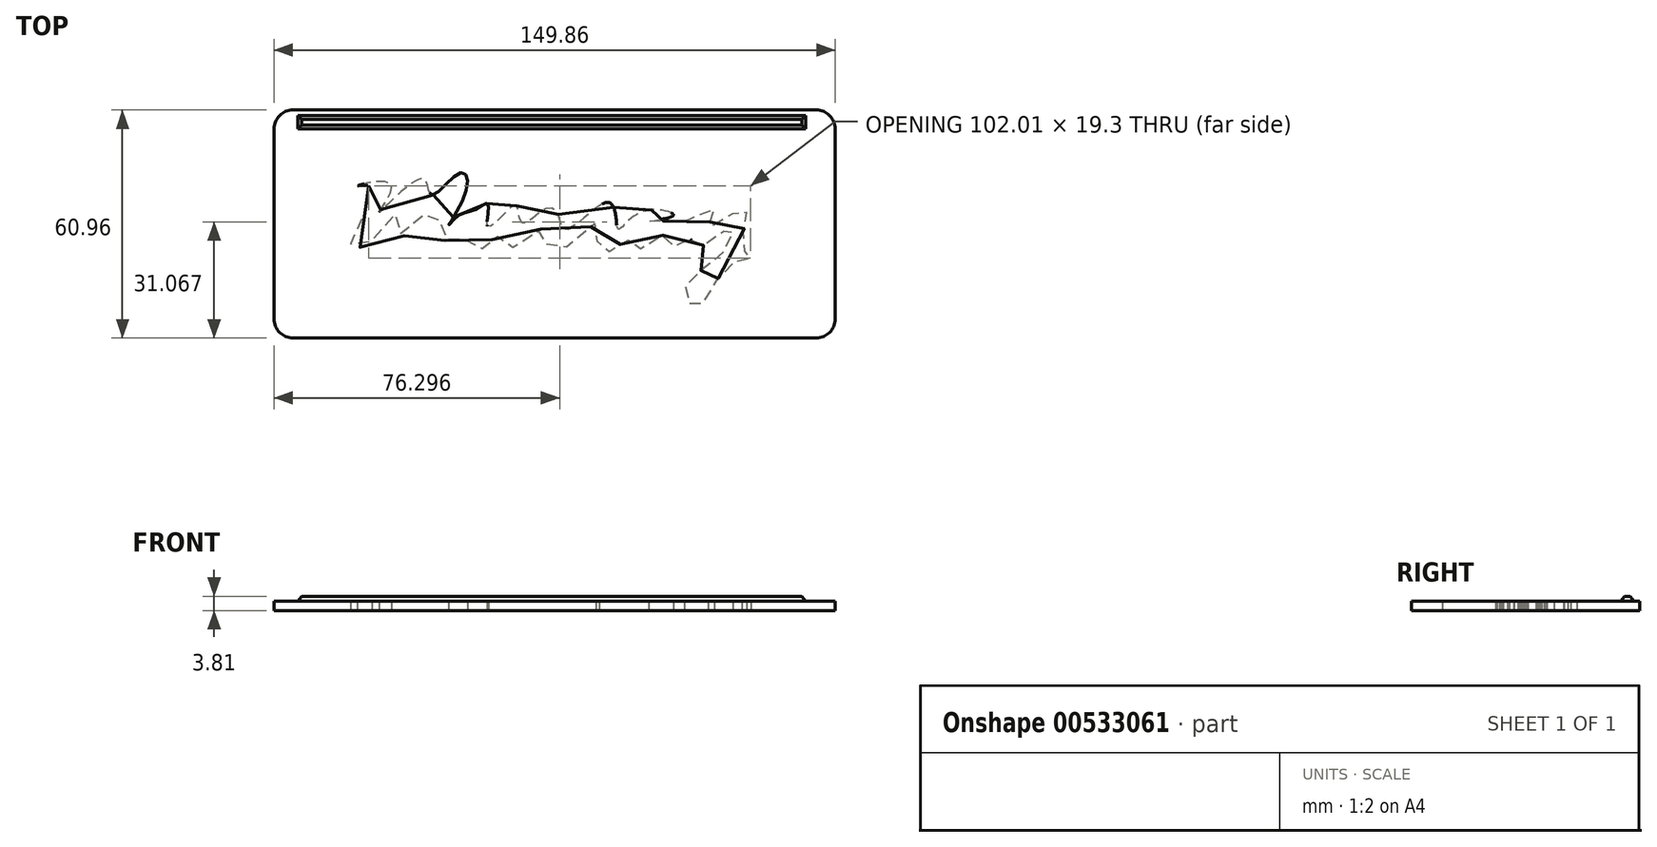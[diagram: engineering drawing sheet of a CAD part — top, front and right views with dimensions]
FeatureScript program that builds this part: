
annotation { "Feature Type Name" : "Feature", "Feature Type Description" : "" }
export const myFeature = defineFeature(function(context is Context, id is Id, definition is map)
    precondition{}
    {
        {
            var Q0;
            Q0=qCreatedBy(makeId("Top.planeOp"),FACE);
            var sketch = newSketch(context, id + "F0", { "sketchPlane" : qUnion([Q0])});
            skLineSegment(sketch, "E0.bottom", {"start": v(69.85, -25.4) * mm, "end": v(-69.85, -25.4) * mm, "construction": true});
            skLineSegment(sketch, "E0.top", {"start": v(69.85, 25.4) * mm, "end": v(-69.85, 25.4) * mm, "construction": true});
            skLineSegment(sketch, "E0.left", {"start": v(69.85, -25.4) * mm, "end": v(69.85, 25.4) * mm, "construction": true});
            skLineSegment(sketch, "E0.right", {"start": v(-69.85, -25.4) * mm, "end": v(-69.85, 25.4) * mm, "construction": true});
            skPoint(sketch, "E0.middle", {"position": v(0, 0) * mm});
            skArc(sketch, "E1", {"start": v(-64.77, 25.4) * mm, "mid": v(-73.44, 29) * mm, "end": v(-69.85, 20.32) * mm});
            skArc(sketch, "E2", {"start": v(69.85, 20.32) * mm, "mid": v(73.44, 29) * mm, "end": v(64.77, 25.4) * mm});
            skArc(sketch, "E3", {"start": v(64.77, -25.4) * mm, "mid": v(73.44, -29) * mm, "end": v(69.85, -20.32) * mm});
            skArc(sketch, "E4", {"start": v(-69.85, -20.32) * mm, "mid": v(-73.44, -29) * mm, "end": v(-64.77, -25.4) * mm});
            skLineSegment(sketch, "E5", {"start": v(-74.93, 25.4) * mm, "end": v(-74.93, -25.4) * mm});
            skLineSegment(sketch, "E6", {"start": v(-69.85, -30.48) * mm, "end": v(69.85, -30.48) * mm});
            skLineSegment(sketch, "E7", {"start": v(74.93, -25.4) * mm, "end": v(74.93, 25.4) * mm});
            skLineSegment(sketch, "E8", {"start": v(69.85, 30.48) * mm, "end": v(-69.85, 30.48) * mm});
            skSolve(sketch);
        }
        {
            var Q0;
            {var subQ0=sQuery(id+"F0.wireOp",EDGE,"E5");Q0=makeQuery(id+"F0.imprint","IMPRINT",FACE,{"disambiguationData":[TD([[makeQuery(id+"F0.imprint","IMPRINT",EDGE,{"derivedFrom":subQ0}),1.0]])]});}
            extrude(context, id + "F1", {"entities" : qUnion([Q0]), "depth" : 2.54 * mm, "offsetDistance" : 25.4 * mm});
        }
        {
            var Q0;
            Q0=makeQuery(id+"F1.opExtrude","CAP_FACE",FACE,{"disambiguationData":[OSD([sQuery(id+"F0.wireOp",EDGE,"E1"),sQuery(id+"F0.wireOp",EDGE,"E2"),sQuery(id+"F0.wireOp",EDGE,"E3"),sQuery(id+"F0.wireOp",EDGE,"E4"),sQuery(id+"F0.wireOp",EDGE,"E5"),sQuery(id+"F0.wireOp",EDGE,"E6"),sQuery(id+"F0.wireOp",EDGE,"E7"),sQuery(id+"F0.wireOp",EDGE,"E8")])],"isStart":false});
            var sketch = newSketch(context, id + "F2", { "sketchPlane" : qUnion([Q0])});
            skFitSpline(sketch, "E9", {"points": [v(-49.64, 10.24) * mm, v(-49.64, 5.53) * mm, v(-54.35, -5.98) * mm, v(-47.9, -3.65) * mm, v(-41.82, 2.67) * mm, v(-40.58, -3.16) * mm, v(-31.77, 4.9) * mm, v(-30.15, -4.65) * mm, v(-25.88, -2.05) * mm, v(-23.15, -5.98) * mm, v(-18.44, -5.98) * mm, v(-15.33, -3.16) * mm, v(-13.6, -5.98) * mm, v(-5.65, -3.29) * mm, v(-3.3, -1.3) * mm, v(-1.44, -7.26) * mm, v(7.62, -2.42) * mm, v(11.84, 0.19) * mm, v(11.35, -7.5) * mm, v(16.8, -5.98) * mm, v(19.78, -4.28) * mm, v(21.03, -5.98) * mm, v(24.62, -5.98) * mm, v(29.34, -3.04) * mm, v(31.57, -5.98) * mm, v(35.42, -3.16) * mm, v(38.15, -5.98) * mm, v(46.96, -1.06) * mm, v(45.1, -7.5) * mm, v(34.68, -17.31) * mm, v(38.15, -22.15) * mm, v(46.84, -10.73) * mm, v(52.42, -9) * mm, v(50.19, -5.98) * mm, v(51.18, 3.16) * mm, v(44.1, 0.8) * mm, v(41, -0.8) * mm, v(42.62, 3.78) * mm, v(35.42, 0.8) * mm, v(32.63, 0.67) * mm, v(25.13, 0.76) * mm, v(31.64, 2.19) * mm, v(28.24, 3.75) * mm, v(20.4, 1.53) * mm, v(17.05, -1.43) * mm, v(16.3, 2.42) * mm, v(13.83, 5.77) * mm, v(2.9, -1.55) * mm, v(0.92, 2.67) * mm, v(-2.55, 4.03) * mm, v(-8.63, 0.19) * mm, v(-10.12, 4.78) * mm, v(-13.35, 2.8) * mm, v(-17.94, -0.56) * mm, v(-17.82, 5.27) * mm, v(-21.41, 3.78) * mm, v(-25.63, 2.3) * mm, v(-28.36, -0.31) * mm, v(-23.52, 9.24) * mm, v(-25.14, 13.71) * mm, v(-32.95, 7.76) * mm, v(-35.19, 12.1) * mm, v(-46.85, 3.16) * mm, v(-43.75, 10.49) * mm, v(-52.68, 10.24) * mm, v(-49.64, 10.24) * mm]});
            skLineSegment(sketch, "E10.bottom", {"start": v(-68.62, 29.05) * mm, "end": v(67.08, 29.05) * mm});
            skLineSegment(sketch, "E10.top", {"start": v(-68.62, 25.4) * mm, "end": v(67.08, 25.4) * mm});
            skLineSegment(sketch, "E10.left", {"start": v(-68.62, 29.05) * mm, "end": v(-68.62, 25.4) * mm});
            skLineSegment(sketch, "E10.right", {"start": v(67.08, 29.05) * mm, "end": v(67.08, 25.4) * mm});
            skSolve(sketch);
        }
        {
            var Q0;
            Q0=makeQuery(id+"F2.imprint","IMPRINT",FACE,{"disambiguationData":[TD([[makeQuery(id+"F2.imprint","IMPRINT",EDGE,{"derivedFrom":sQuery(id+"F2.wireOp",EDGE,"E10.bottom")}),-1.0]])]});
            extrude(context, id + "F3", {"entities" : qUnion([Q0]), "operationType" : NewBodyOperationType.ADD, "depth" : 1.27 * mm, "offsetDistance" : 25.4 * mm, "hasDraft" : true, "draftAngle" : 40 * degree, "draftPullDirection" : true});
        }
        {
            var Q0;
            Q0=makeQuery(id+"F2.imprint","IMPRINT",FACE,{"disambiguationData":[TD([[makeQuery(id+"F2.imprint","IMPRINT",EDGE,{"derivedFrom":sQuery(id+"F2.wireOp",EDGE,"E9")}),1.0]])]});
            extrude(context, id + "F4", {"entities" : qUnion([Q0]), "operationType" : NewBodyOperationType.REMOVE, "oppositeDirection" : true, "depth" : 25.4 * mm, "offsetDistance" : 25.4 * mm});
        }
    });
